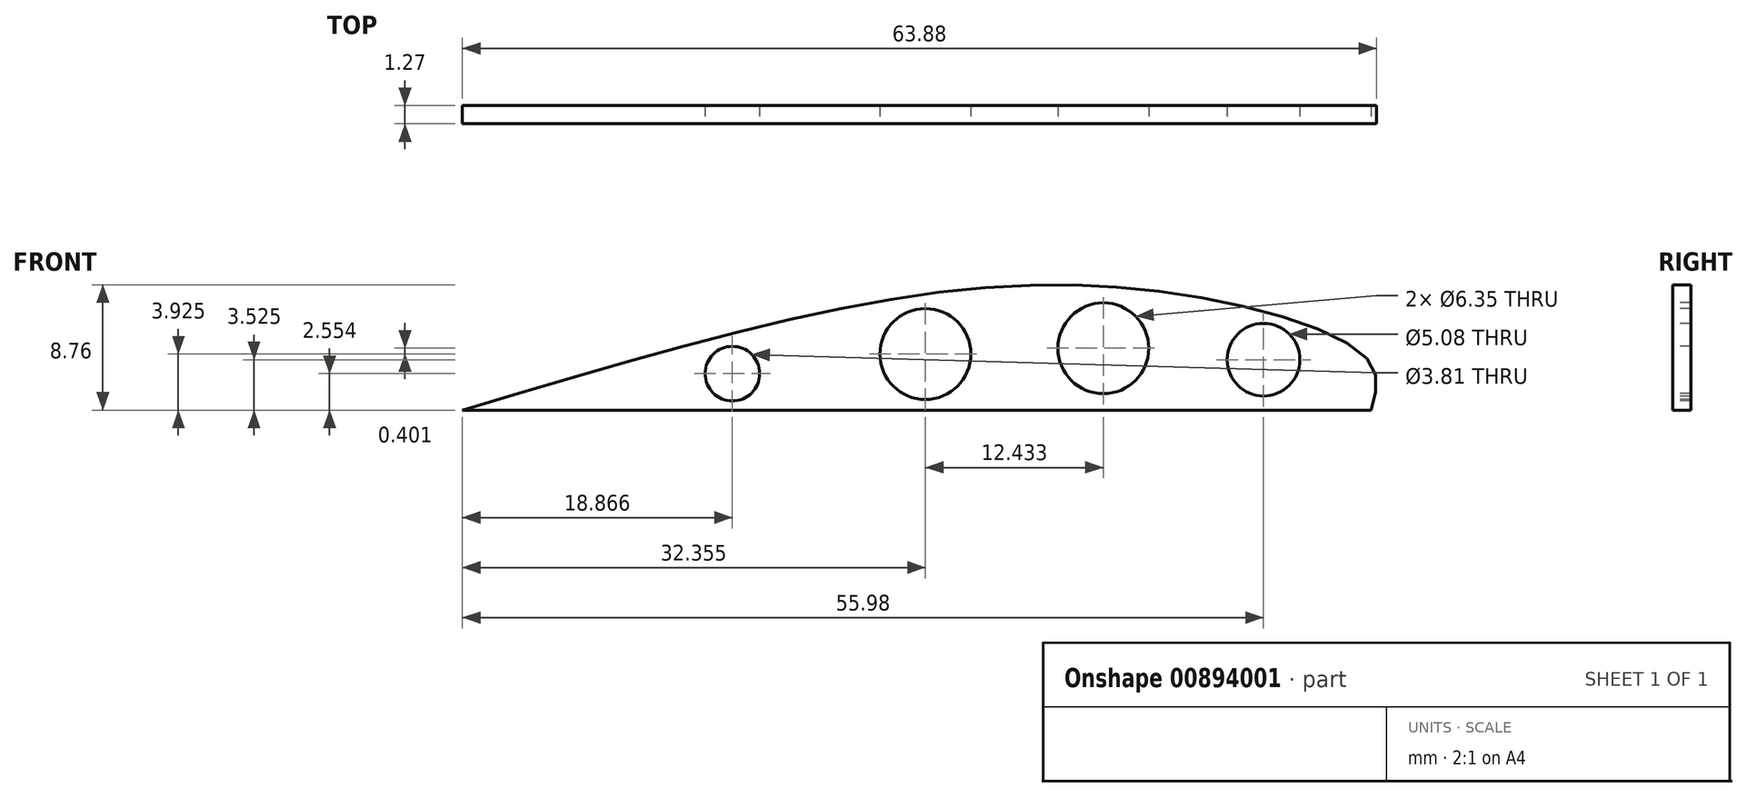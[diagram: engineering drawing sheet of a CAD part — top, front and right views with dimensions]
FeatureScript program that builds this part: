
annotation { "Feature Type Name" : "Feature", "Feature Type Description" : "" }
export const myFeature = defineFeature(function(context is Context, id is Id, definition is map)
    precondition{}
    {
        {
            var Q0;
            Q0=qCreatedBy(makeId("Front.planeOp"),FACE);
            var sketch = newSketch(context, id + "F0", { "sketchPlane" : qUnion([Q0])});
            skLineSegment(sketch, "E0", {"start": v(0, 0) * mm, "end": v(63.5, 0) * mm});
            skFitSpline(sketch, "E1", {"points": [v(63.5, 0) * mm, v(63.5, 3.24) * mm, v(52.03, 7.79) * mm, v(31.36, 7.97) * mm, v(0, 0) * mm], "startDerivative": vector(8.6, 28.8) * mm, "endDerivative": vector(-89.9, -26.91) * mm});
            skSolve(sketch);
        }
        {
            var Q0;
            Q0=makeQuery(id+"F0.imprint","IMPRINT",FACE,{"disambiguationData":[TD([[makeQuery(id+"F0.imprint","IMPRINT",EDGE,{"derivedFrom":sQuery(id+"F0.wireOp",EDGE,"E0")}),1.0]])]});
            var Q1;
            Q1 = qSketchRegion(id + "F2", true);
            extrude(context, id + "F1", {"entities" : qUnion([Q0, Q1]), "oppositeDirection" : true, "depth" : 1.27 * mm, "offsetDistance" : 25.4 * mm});
        }
        {
            var Q0;
            Q0=qCreatedBy(makeId("Front.planeOp"),FACE);
            var sketch = newSketch(context, id + "F2", { "sketchPlane" : qUnion([Q0])});
            skPoint(sketch, "E2", {"position": v(18.87, 2.55) * mm});
            skPoint(sketch, "E3", {"position": v(32.36, 3.92) * mm});
            skPoint(sketch, "E4", {"position": v(44.79, 4.33) * mm});
            skPoint(sketch, "E5", {"position": v(55.98, 3.53) * mm});
            skSolve(sketch);
        }
        {
            var Q0;
            Q0=sQuery(id+"F2.wireOp",VERTEX,"E5");
            var Q1;
            Q1=makeQuery(id+"F1.opExtrude","SWEPT_BODY",BODY,{"disambiguationData":[OSD([sQuery(id+"F0.wireOp",EDGE,"E0"),sQuery(id+"F0.wireOp",EDGE,"E1")])]});
            hole(context, id + "F3", {"style" : HoleStyle.SIMPLE, "endStyle" : HoleEndStyle.THROUGH, "holeDiameter" : 5.08 * mm, "majorDiameter" : 6.35 * mm, "isTappedThrough" : true, "tappedDepth" : 12.7 * mm, "tapClearance" : 3, "locations" : qUnion([Q0]), "scope" : qUnion([Q1])});
        }
        {
            var Q0;
            Q0=sQuery(id+"F2.wireOp",VERTEX,"E4");
            var Q1;
            Q1=sQuery(id+"F2.wireOp",VERTEX,"E3");
            var Q2;
            Q2=makeQuery(id+"F1.opExtrude","SWEPT_BODY",BODY,{"disambiguationData":[OSD([sQuery(id+"F0.wireOp",EDGE,"E0"),sQuery(id+"F0.wireOp",EDGE,"E1")])]});
            hole(context, id + "F4", {"style" : HoleStyle.SIMPLE, "endStyle" : HoleEndStyle.THROUGH, "holeDiameter" : 6.35 * mm, "majorDiameter" : 6.35 * mm, "isTappedThrough" : true, "tappedDepth" : 12.7 * mm, "tapClearance" : 3, "locations" : qUnion([Q0, Q1]), "scope" : qUnion([Q2])});
        }
        {
            var Q0;
            Q0=sQuery(id+"F2.wireOp",VERTEX,"E2");
            var Q1;
            Q1=makeQuery(id+"F1.opExtrude","SWEPT_BODY",BODY,{"disambiguationData":[OSD([sQuery(id+"F0.wireOp",EDGE,"E0"),sQuery(id+"F0.wireOp",EDGE,"E1")])]});
            hole(context, id + "F5", {"style" : HoleStyle.SIMPLE, "endStyle" : HoleEndStyle.THROUGH, "holeDiameter" : 3.8 * mm, "majorDiameter" : 6.35 * mm, "isTappedThrough" : true, "tappedDepth" : 12.7 * mm, "tapClearance" : 3, "locations" : qUnion([Q0]), "scope" : qUnion([Q1])});
        }
    });
